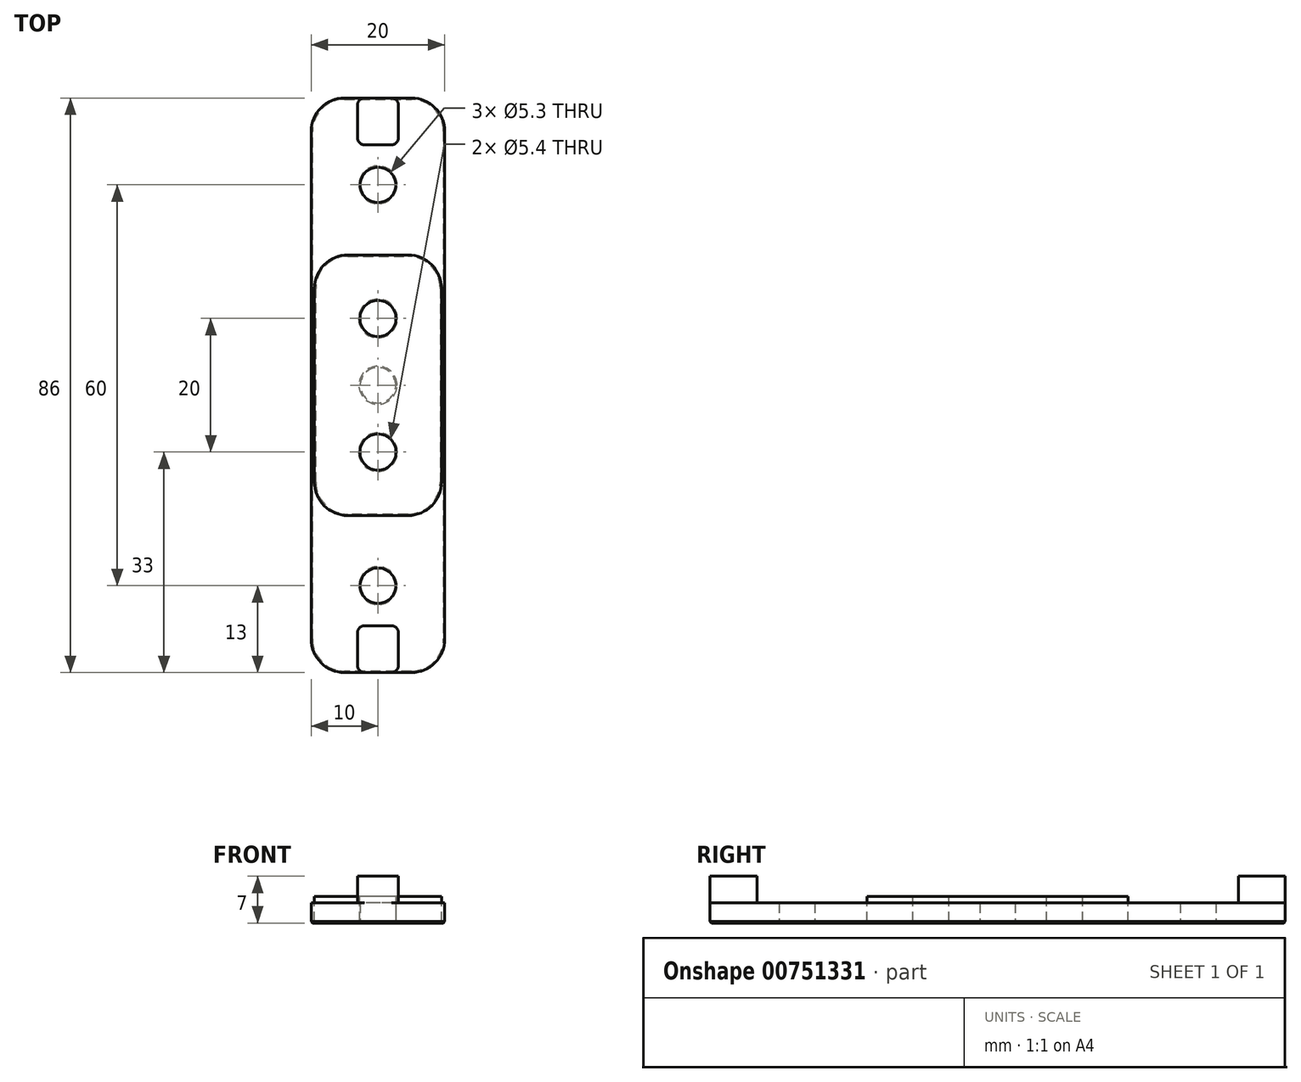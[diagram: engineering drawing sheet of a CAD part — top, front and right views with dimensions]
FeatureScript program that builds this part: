
annotation { "Feature Type Name" : "Feature", "Feature Type Description" : "" }
export const myFeature = defineFeature(function(context is Context, id is Id, definition is map)
    precondition{}
    {
        {
            var Q0;
            Q0=qCreatedBy(makeId("Top.planeOp"),FACE);
            var sketch = newSketch(context, id + "F0", { "sketchPlane" : qUnion([Q0])});
            skLineSegment(sketch, "E0.bottom", {"start": v(9.5, 19.5) * mm, "end": v(-9.5, 19.5) * mm});
            skLineSegment(sketch, "E0.top", {"start": v(9.5, -19.5) * mm, "end": v(-9.5, -19.5) * mm});
            skLineSegment(sketch, "E0.left", {"start": v(9.5, 19.5) * mm, "end": v(9.5, -19.5) * mm});
            skLineSegment(sketch, "E0.right", {"start": v(-9.5, 19.5) * mm, "end": v(-9.5, -19.5) * mm});
            skPoint(sketch, "E0.middle", {"position": v(0, 0) * mm});
            skCircle(sketch, "E1", {"center": v(0, 10) * mm, "radius": 2.5 * mm, "construction": true});
            skCircle(sketch, "E2.MirrorC", {"center": v(0, -10) * mm, "radius": 2.5 * mm, "construction": true});
            skCircle(sketch, "E3.0", {"center": v(0, 10) * mm, "radius": 2.7 * mm});
            skCircle(sketch, "E4.0", {"center": v(0, -10) * mm, "radius": 2.7 * mm});
            skSolve(sketch);
        }
        {
            var Q0;
            Q0=qCreatedBy(makeId("Front.planeOp"),FACE);
            var sketch = newSketch(context, id + "F1", { "sketchPlane" : qUnion([Q0])});
            skLineSegment(sketch, "E5", {"start": v(0, 0) * mm, "end": v(0, 4) * mm});
            skSolve(sketch);
        }
        {
            var Q0;
            Q0 = qSketchRegion(id + "F0", true);
            var Q1;
            Q1=sQuery(id+"F1.wireOp",EDGE,"E5");
            sweep(context, id + "F2", {"profiles" : qUnion([Q0]), "path" : qUnion([Q1])});
        }
        {
            var Q0;
            Q0=makeQuery(id+"F2.opSweep","SWEPT_EDGE",EDGE,{"disambiguationData":[OSD([sQuery(id+"F0.wireOp",EDGE,"E0.top"),sQuery(id+"F0.wireOp",EDGE,"E0.right"),sQuery(id+"F1.wireOp",EDGE,"E5")])]});
            var Q1;
            Q1=makeQuery(id+"F2.opSweep","SWEPT_EDGE",EDGE,{"disambiguationData":[OSD([sQuery(id+"F0.wireOp",EDGE,"E0.top"),sQuery(id+"F0.wireOp",EDGE,"E0.left"),sQuery(id+"F1.wireOp",EDGE,"E5")])]});
            var Q2;
            Q2=makeQuery(id+"F2.opSweep","SWEPT_EDGE",EDGE,{"disambiguationData":[OSD([sQuery(id+"F0.wireOp",EDGE,"E0.bottom"),sQuery(id+"F0.wireOp",EDGE,"E0.right"),sQuery(id+"F1.wireOp",EDGE,"E5")])]});
            var Q3;
            Q3=makeQuery(id+"F2.opSweep","SWEPT_EDGE",EDGE,{"disambiguationData":[OSD([sQuery(id+"F0.wireOp",EDGE,"E0.bottom"),sQuery(id+"F0.wireOp",EDGE,"E0.left"),sQuery(id+"F1.wireOp",EDGE,"E5")])]});
            fillet(context, id + "F3", {"entities" : qUnion([Q0, Q1, Q2, Q3]), "radius" : 5 * mm, "allowEdgeOverflow" : false});
        }
        {
            var Q0;
            Q0=qCreatedBy(makeId("Top.planeOp"),FACE);
            var sketch = newSketch(context, id + "F4", { "sketchPlane" : qUnion([Q0])});
            skLineSegment(sketch, "E6.bottom", {"start": v(10, 43) * mm, "end": v(-10, 43) * mm});
            skLineSegment(sketch, "E6.top", {"start": v(10, -43) * mm, "end": v(-10, -43) * mm});
            skLineSegment(sketch, "E6.left", {"start": v(10, 43) * mm, "end": v(10, -43) * mm});
            skLineSegment(sketch, "E6.right", {"start": v(-10, 43) * mm, "end": v(-10, -43) * mm});
            skPoint(sketch, "E6.middle", {"position": v(0, 0) * mm});
            skCircle(sketch, "E7", {"center": v(0, 30) * mm, "radius": 2.5 * mm, "construction": true});
            skCircle(sketch, "E8.MirrorC", {"center": v(0, -30) * mm, "radius": 2.5 * mm, "construction": true});
            skCircle(sketch, "E9.0", {"center": v(0, 30) * mm, "radius": 2.65 * mm});
            skCircle(sketch, "E10.0", {"center": v(0, -30) * mm, "radius": 2.65 * mm});
            skCircle(sketch, "E11", {"center": v(0, 0) * mm, "radius": 2.5 * mm, "construction": true});
            skCircle(sketch, "E12.0", {"center": v(0, 0) * mm, "radius": 2.65 * mm});
            skSolve(sketch);
        }
        {
            var Q0;
            Q0 = qSketchRegion(id + "F4", true);
            extrude(context, id + "F5", {"entities" : qUnion([Q0]), "depth" : 3 * mm, "offsetDistance" : 25 * mm});
        }
        {
            var Q0;
            Q0=makeQuery(id+"F5.opExtrude","CAP_FACE",FACE,{"disambiguationData":[OSD([sQuery(id+"F4.wireOp",EDGE,"E6.bottom"),sQuery(id+"F4.wireOp",EDGE,"E6.top"),sQuery(id+"F4.wireOp",EDGE,"E6.left"),sQuery(id+"F4.wireOp",EDGE,"E6.right"),sQuery(id+"F4.wireOp",EDGE,"E9.0"),sQuery(id+"F4.wireOp",EDGE,"E10.0")])],"isStart":false});
            var sketch = newSketch(context, id + "F6", { "sketchPlane" : qUnion([Q0])});
            skLineSegment(sketch, "E13.0", {"start": v(10, 43) * mm, "end": v(-10, 43) * mm, "construction": true});
            skLineSegment(sketch, "E14.0", {"start": v(10, -43) * mm, "end": v(-10, -43) * mm, "construction": true});
            skLineSegment(sketch, "E15.bottom", {"start": v(3.05, 43) * mm, "end": v(-3.05, 43) * mm});
            skLineSegment(sketch, "E15.top", {"start": v(3.05, 36) * mm, "end": v(-3.05, 36) * mm});
            skLineSegment(sketch, "E15.left", {"start": v(3.05, 43) * mm, "end": v(3.05, 36) * mm});
            skLineSegment(sketch, "E15.right", {"start": v(-3.05, 43) * mm, "end": v(-3.05, 36) * mm});
            skPoint(sketch, "E15.middle", {"position": v(0, 39.5) * mm});
            skPoint(sketch, "E16.0", {"position": v(0, 30) * mm});
            skLineSegment(sketch, "E17.MirrorCS", {"start": v(-3.05, -43) * mm, "end": v(-3.05, -36) * mm});
            skLineSegment(sketch, "E18.MirrorCS", {"start": v(3.05, -36) * mm, "end": v(-3.05, -36) * mm});
            skLineSegment(sketch, "E19.MirrorCS", {"start": v(3.05, -43) * mm, "end": v(3.05, -36) * mm});
            skLineSegment(sketch, "E20.MirrorCS", {"start": v(3.05, -43) * mm, "end": v(-3.05, -43) * mm});
            skSolve(sketch);
        }
        {
            var Q0;
            Q0 = qSketchRegion(id + "F6", true);
            extrude(context, id + "F7", {"entities" : qUnion([Q0]), "operationType" : NewBodyOperationType.ADD, "depth" : 4 * mm, "offsetDistance" : 25 * mm});
        }
        {
            var Q0;
            Q0=makeQuery(id+"F5.opExtrude","SWEPT_EDGE",EDGE,{"disambiguationData":[OSD([sQuery(id+"F4.wireOp",EDGE,"E6.top"),sQuery(id+"F4.wireOp",EDGE,"E6.right")])]});
            var Q1;
            Q1=makeQuery(id+"F5.opExtrude","SWEPT_EDGE",EDGE,{"disambiguationData":[OSD([sQuery(id+"F4.wireOp",EDGE,"E6.top"),sQuery(id+"F4.wireOp",EDGE,"E6.left")])]});
            var Q2;
            Q2=makeQuery(id+"F5.opExtrude","SWEPT_EDGE",EDGE,{"disambiguationData":[OSD([sQuery(id+"F4.wireOp",EDGE,"E6.bottom"),sQuery(id+"F4.wireOp",EDGE,"E6.right")])]});
            var Q3;
            Q3=makeQuery(id+"F5.opExtrude","SWEPT_EDGE",EDGE,{"disambiguationData":[OSD([sQuery(id+"F4.wireOp",EDGE,"E6.bottom"),sQuery(id+"F4.wireOp",EDGE,"E6.left")])]});
            fillet(context, id + "F8", {"entities" : qUnion([Q0, Q1, Q2, Q3]), "radius" : 5 * mm, "allowEdgeOverflow" : false});
        }
        {
            var Q0;
            Q0=makeQuery(id+"F7.opExtrude","SWEPT_EDGE",EDGE,{"disambiguationData":[OSD([sQuery(id+"F4.wireOp",EDGE,"E6.top"),sQuery(id+"F6.wireOp",EDGE,"E17.MirrorCS"),sQuery(id+"F6.wireOp",EDGE,"E20.MirrorCS")])]});
            var Q1;
            Q1=makeQuery(id+"F7.opExtrude","SWEPT_EDGE",EDGE,{"disambiguationData":[OSD([sQuery(id+"F4.wireOp",EDGE,"E6.top"),sQuery(id+"F6.wireOp",EDGE,"E19.MirrorCS"),sQuery(id+"F6.wireOp",EDGE,"E20.MirrorCS")])]});
            var Q2;
            Q2=makeQuery(id+"F7.opExtrude","SWEPT_EDGE",EDGE,{"disambiguationData":[OSD([sQuery(id+"F6.wireOp",EDGE,"E17.MirrorCS"),sQuery(id+"F6.wireOp",EDGE,"E18.MirrorCS")])]});
            var Q3;
            Q3=makeQuery(id+"F7.opExtrude","SWEPT_EDGE",EDGE,{"disambiguationData":[OSD([sQuery(id+"F6.wireOp",EDGE,"E18.MirrorCS"),sQuery(id+"F6.wireOp",EDGE,"E19.MirrorCS")])]});
            var Q4;
            Q4=makeQuery(id+"F7.opExtrude","SWEPT_EDGE",EDGE,{"disambiguationData":[OSD([sQuery(id+"F4.wireOp",EDGE,"E6.bottom"),sQuery(id+"F6.wireOp",EDGE,"E15.bottom"),sQuery(id+"F6.wireOp",EDGE,"E15.left")])]});
            var Q5;
            Q5=makeQuery(id+"F7.opExtrude","SWEPT_EDGE",EDGE,{"disambiguationData":[OSD([sQuery(id+"F6.wireOp",EDGE,"E15.top"),sQuery(id+"F6.wireOp",EDGE,"E15.left")])]});
            var Q6;
            Q6=makeQuery(id+"F7.opExtrude","SWEPT_EDGE",EDGE,{"disambiguationData":[OSD([sQuery(id+"F6.wireOp",EDGE,"E15.top"),sQuery(id+"F6.wireOp",EDGE,"E15.right")])]});
            var Q7;
            Q7=makeQuery(id+"F7.opExtrude","SWEPT_EDGE",EDGE,{"disambiguationData":[OSD([sQuery(id+"F4.wireOp",EDGE,"E6.bottom"),sQuery(id+"F6.wireOp",EDGE,"E15.bottom"),sQuery(id+"F6.wireOp",EDGE,"E15.right")])]});
            fillet(context, id + "F9", {"entities" : qUnion([Q0, Q1, Q2, Q3, Q4, Q5, Q6, Q7]), "radius" : 1 * mm, "allowEdgeOverflow" : false});
        }
        {
            var Q0;
            Q0=makeQuery(id+"F2.opSweep","CAP_FACE",FACE,{"disambiguationData":[OSD([sQuery(id+"F0.wireOp",EDGE,"E0.bottom"),sQuery(id+"F0.wireOp",EDGE,"E0.top"),sQuery(id+"F0.wireOp",EDGE,"E0.left"),sQuery(id+"F0.wireOp",EDGE,"E0.right"),sQuery(id+"F0.wireOp",EDGE,"E3.0"),sQuery(id+"F0.wireOp",EDGE,"E4.0"),sQuery(id+"F1.wireOp",VERTEX,"E5.start")])],"isStart":true});
            var Q1;
            Q1=makeQuery(id+"F5.opExtrude","CAP_FACE",FACE,{"disambiguationData":[OSD([sQuery(id+"F4.wireOp",EDGE,"E6.bottom"),sQuery(id+"F4.wireOp",EDGE,"E6.top"),sQuery(id+"F4.wireOp",EDGE,"E6.left"),sQuery(id+"F4.wireOp",EDGE,"E6.right"),sQuery(id+"F4.wireOp",EDGE,"E9.0"),sQuery(id+"F4.wireOp",EDGE,"E10.0")])],"isStart":true});
            chamfer(context, id + "F10", {"entities" : qUnion([Q0, Q1]), "width" : 0.2 * mm, "tangentPropagation" : true});
        }
    });
